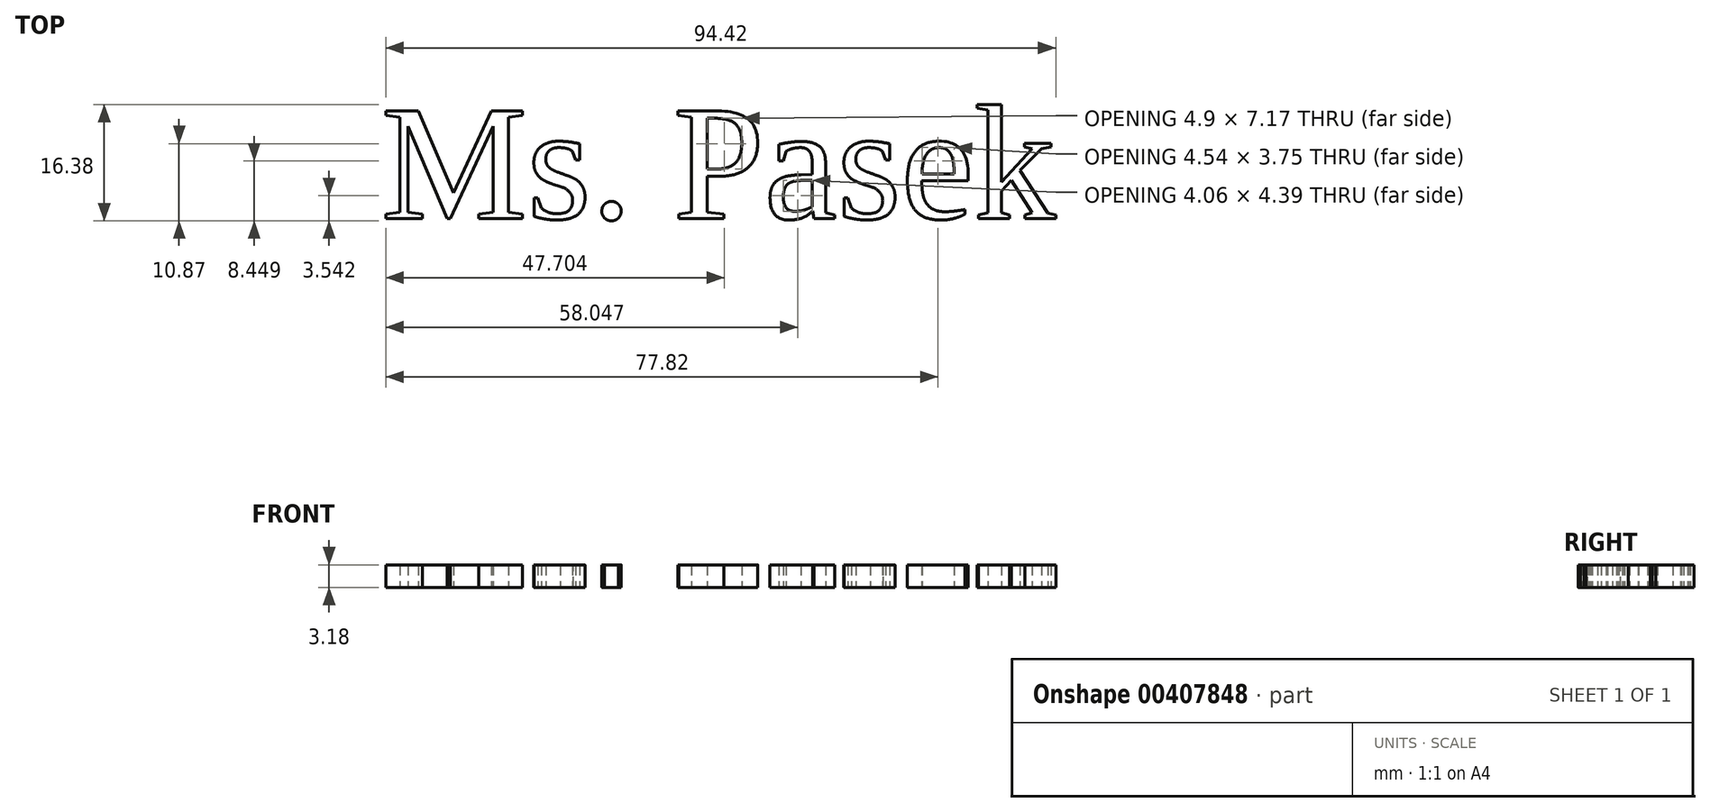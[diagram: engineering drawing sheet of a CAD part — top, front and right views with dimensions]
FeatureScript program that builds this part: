
annotation { "Feature Type Name" : "Feature", "Feature Type Description" : "" }
export const myFeature = defineFeature(function(context is Context, id is Id, definition is map)
    precondition{}
    {
        {
            var Q0;
            Q0=qCreatedBy(makeId("Top.planeOp"),FACE);
            var sketch = newSketch(context, id + "F0", { "sketchPlane" : qUnion([Q0])});
            skText(sketch, "E0", { "text": "Ms. Pasek", "fontName": "Tinos-Regular.ttf"});
            const initialGuessF0  = {"E0": [0, 0, 1, 0, 0.01665]};
            skSetInitialGuess(sketch, initialGuessF0);
            skSolve(sketch);
        }
        {
            var Q0;
            Q0 = qSketchRegion(id + "F0", true);
            extrude(context, id + "F1", {"entities" : qUnion([Q0]), "depth" : 3.17 * mm});
        }
    });
